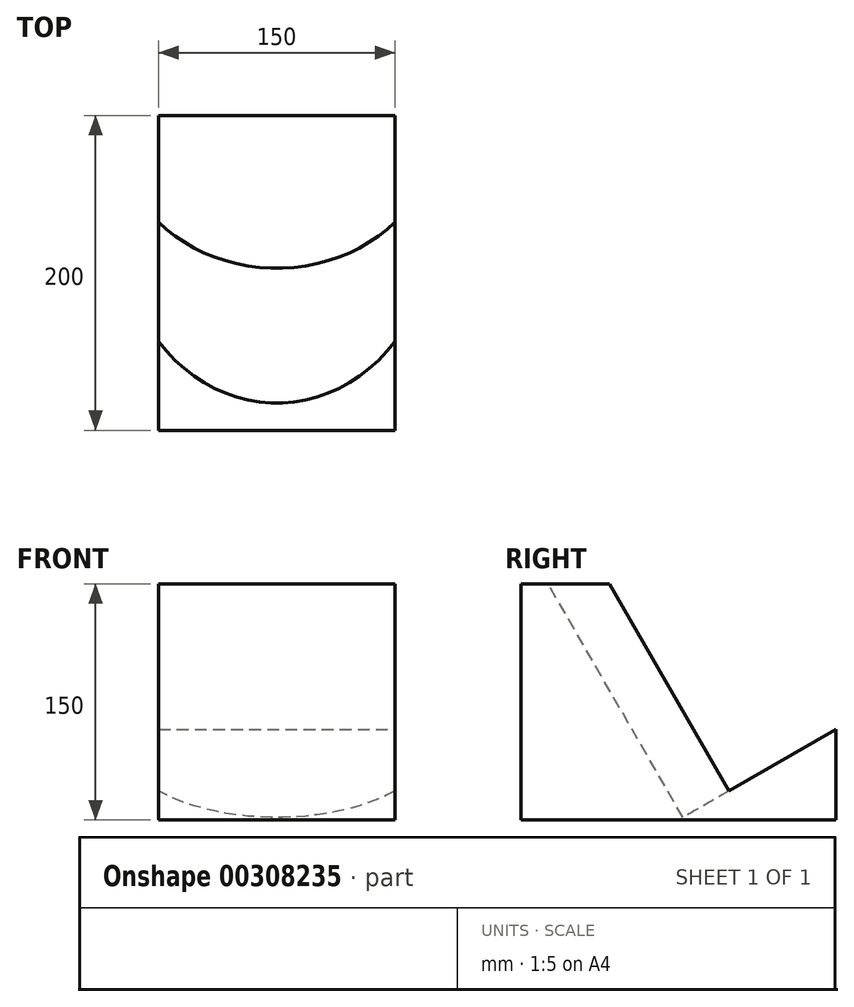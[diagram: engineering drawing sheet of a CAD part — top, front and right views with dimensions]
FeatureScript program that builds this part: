
annotation { "Feature Type Name" : "Feature", "Feature Type Description" : "" }
export const myFeature = defineFeature(function(context is Context, id is Id, definition is map)
    precondition{}
    {
        {
            var Q0;
            Q0=qCreatedBy(makeId("Top.planeOp"),FACE);
            var sketch = newSketch(context, id + "F0", { "sketchPlane" : qUnion([Q0])});
            skLineSegment(sketch, "E0.bottom", {"start": v(75, 100) * mm, "end": v(-75, 100) * mm});
            skLineSegment(sketch, "E0.top", {"start": v(75, -100) * mm, "end": v(-75, -100) * mm});
            skLineSegment(sketch, "E0.left", {"start": v(75, 100) * mm, "end": v(75, -100) * mm});
            skLineSegment(sketch, "E0.right", {"start": v(-75, 100) * mm, "end": v(-75, -100) * mm});
            skPoint(sketch, "E0.middle", {"position": v(0, 0) * mm});
            skSolve(sketch);
        }
        {
            var Q0;
            Q0=makeQuery(id+"F0.imprint","IMPRINT",FACE,{"disambiguationData":[TD([[makeQuery(id+"F0.imprint","IMPRINT",EDGE,{"derivedFrom":sQuery(id+"F0.wireOp",EDGE,"E0.bottom")}),1.0]])]});
            extrude(context, id + "F1", {"entities" : qUnion([Q0]), "depth" : 150 * mm, "offsetDistance" : 25 * mm});
        }
        {
            var Q0;
            Q0=makeQuery(id+"F1.opExtrude","CAP_EDGE",EDGE,{"disambiguationData":[OSD([sQuery(id+"F0.wireOp",EDGE,"E0.bottom")])],"isStart":false});
            cPoint(context, id + "F2", {"entities" : qUnion([Q0]), "parameter" : 0.5});
        }
        {
            var Q0;
            Q0=makeQuery(id+"F1.opExtrude","CAP_EDGE",EDGE,{"disambiguationData":[OSD([sQuery(id+"F0.wireOp",EDGE,"E0.top")])],"isStart":false});
            var Q1;
            Q1 = qCreatedBy(id + "F2" ,VERTEX);
            cPlane(context, id + "F3", {"entities" : qUnion([Q0, Q1]), "cplaneType" : CPlaneType.LINE_ANGLE, "offset" : 25 * mm, "angle" : 30 * degree, "oppositeDirection" : true, "width" : 150 * mm, "height" : 150 * mm});
        }
        {
            var Q0;
            Q0=qCreatedBy(id+"F3.planeOp",FACE);
            var sketch = newSketch(context, id + "F4", { "sketchPlane" : qUnion([Q0])});
            skLineSegment(sketch, "E1.0", {"start": v(75, -161.6) * mm, "end": v(75, 11.6) * mm, "construction": true});
            skLineSegment(sketch, "E2.0", {"start": v(75, 11.6) * mm, "end": v(-75, 11.6) * mm, "construction": true});
            skCircle(sketch, "E3", {"center": v(0, -103.4) * mm, "radius": 100 * mm});
            skSolve(sketch);
        }
        {
            var Q0;
            Q0=makeQuery(id+"F4.imprint","IMPRINT",FACE,{"disambiguationData":[TD([[makeQuery(id+"F4.imprint","IMPRINT",EDGE,{"derivedFrom":sQuery(id+"F4.wireOp",EDGE,"E3")}),1.0]])]});
            extrude(context, id + "F5", {"entities" : qUnion([Q0]), "operationType" : NewBodyOperationType.REMOVE, "depth" : 180 * mm, "offsetDistance" : 25 * mm});
        }
    });
